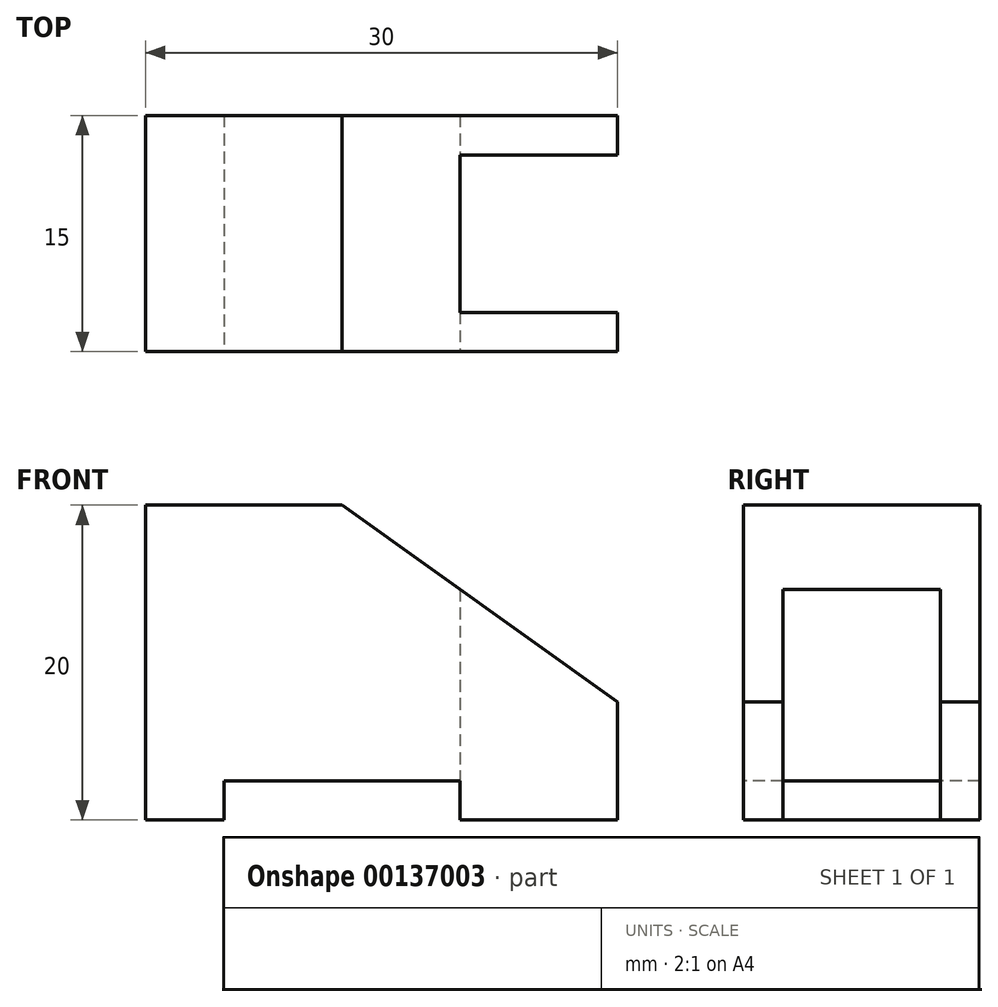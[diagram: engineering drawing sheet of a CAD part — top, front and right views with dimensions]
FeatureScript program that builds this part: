
annotation { "Feature Type Name" : "Feature", "Feature Type Description" : "" }
export const myFeature = defineFeature(function(context is Context, id is Id, definition is map)
    precondition{}
    {
        {
            var Q0;
            Q0=qCreatedBy(makeId("Front.planeOp"),FACE);
            var sketch = newSketch(context, id + "F0", { "sketchPlane" : qUnion([Q0])});
            skLineSegment(sketch, "E0", {"start": v(0, 0) * mm, "end": v(0, 20) * mm});
            skLineSegment(sketch, "E1", {"start": v(0, 20) * mm, "end": v(12.5, 20) * mm});
            skLineSegment(sketch, "E2", {"start": v(12.5, 20) * mm, "end": v(30, 7.5) * mm});
            skLineSegment(sketch, "E3", {"start": v(30, 7.5) * mm, "end": v(30, 0) * mm});
            skLineSegment(sketch, "E4", {"start": v(30, 0) * mm, "end": v(20, 0) * mm});
            skLineSegment(sketch, "E5", {"start": v(20, 0) * mm, "end": v(20, 2.5) * mm});
            skLineSegment(sketch, "E6", {"start": v(20, 2.5) * mm, "end": v(5, 2.5) * mm});
            skLineSegment(sketch, "E7", {"start": v(5, 2.5) * mm, "end": v(5, 0) * mm});
            skLineSegment(sketch, "E8", {"start": v(5, 0) * mm, "end": v(0, 0) * mm});
            skSolve(sketch);
        }
        {
            var Q0;
            Q0 = qSketchRegion(id + "F0", true);
            extrude(context, id + "F1", {"entities" : qUnion([Q0]), "oppositeDirection" : true, "depth" : 15 * mm});
        }
        {
            var Q0;
            Q0=makeQuery(id+"F1.opExtrude","SWEPT_FACE",FACE,{"disambiguationData":[OSD([sQuery(id+"F0.wireOp",EDGE,"E4")])]});
            var sketch = newSketch(context, id + "F2", { "sketchPlane" : qUnion([Q0])});
            skLineSegment(sketch, "E9.bottom", {"start": v(20, -2.5) * mm, "end": v(40, -2.5) * mm});
            skLineSegment(sketch, "E9.top", {"start": v(20, -12.5) * mm, "end": v(40, -12.5) * mm});
            skLineSegment(sketch, "E9.left", {"start": v(20, -2.5) * mm, "end": v(20, -12.5) * mm});
            skLineSegment(sketch, "E9.right", {"start": v(40, -2.5) * mm, "end": v(40, -12.5) * mm});
            skPoint(sketch, "E9.middle", {"position": v(30, -7.5) * mm});
            skSolve(sketch);
        }
        {
            var Q0;
            Q0 = qSketchRegion(id + "F2", true);
            var Q1;
            Q1=makeQuery(id+"F1.opExtrude","SWEPT_FACE",FACE,{"disambiguationData":[OSD([sQuery(id+"F0.wireOp",EDGE,"E2")])]});
            extrude(context, id + "F3", {"entities" : qUnion([Q0]), "operationType" : NewBodyOperationType.REMOVE, "endBound" : BoundingType.UP_TO_SURFACE, "oppositeDirection" : true, "endBoundEntityFace" : qUnion([Q1]), "depth" : 25 * mm});
        }
    });
